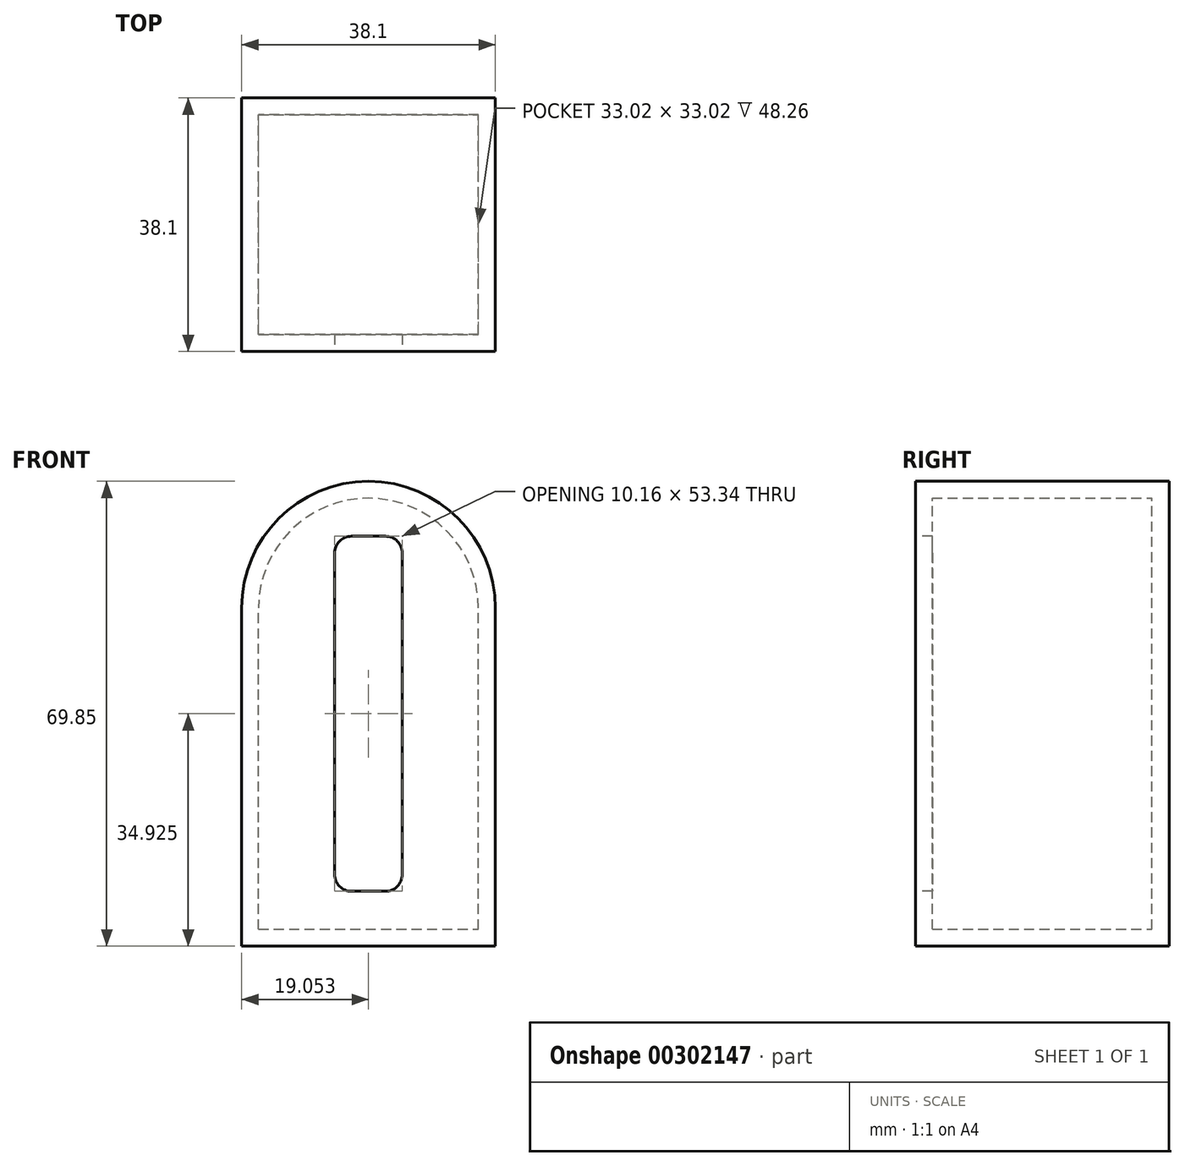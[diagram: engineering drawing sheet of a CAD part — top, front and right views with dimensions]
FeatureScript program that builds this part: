
annotation { "Feature Type Name" : "Feature", "Feature Type Description" : "" }
export const myFeature = defineFeature(function(context is Context, id is Id, definition is map)
    precondition{}
    {
        {
            var Q0;
            Q0=qCreatedBy(makeId("Front.planeOp"),FACE);
            var sketch = newSketch(context, id + "F0", { "sketchPlane" : qUnion([Q0])});
            skLineSegment(sketch, "E0.bottom", {"start": v(-66.24, 0) * mm, "end": v(-28.14, 0) * mm});
            skLineSegment(sketch, "E0.top", {"start": v(-66.24, 50.8) * mm, "end": v(-28.14, 50.8) * mm});
            skLineSegment(sketch, "E0.left", {"start": v(-66.24, 0) * mm, "end": v(-66.24, 50.8) * mm});
            skLineSegment(sketch, "E0.right", {"start": v(-28.14, 0) * mm, "end": v(-28.14, 50.8) * mm});
            skArc(sketch, "E1", {"start": v(-28.14, 50.8) * mm, "mid": v(-47.19, 69.85) * mm, "end": v(-66.24, 50.8) * mm});
            skSolve(sketch);
        }
        {
            var Q0;
            Q0=makeQuery(id+"F0.imprint","IMPRINT",FACE,{"disambiguationData":[TD([[makeQuery(id+"F0.imprint","IMPRINT",EDGE,{"derivedFrom":sQuery(id+"F0.wireOp",EDGE,"E0.bottom")}),1.0]])]});
            var Q1;
            Q1=makeQuery(id+"F0.imprint","IMPRINT",FACE,{"disambiguationData":[TD([[makeQuery(id+"F0.imprint","IMPRINT",EDGE,{"derivedFrom":sQuery(id+"F0.wireOp",EDGE,"E0.top")}),1.0]])]});
            extrude(context, id + "F1", {"entities" : qUnion([Q0, Q1]), "depth" : 38.1 * mm});
        }
        {
            var Q0;
            Q0=makeQuery(id+"F1.opExtrude","CAP_FACE",FACE,{"disambiguationData":[OSD([sQuery(id+"F0.wireOp",EDGE,"E0.bottom"),sQuery(id+"F0.wireOp",EDGE,"E0.left"),sQuery(id+"F0.wireOp",EDGE,"E0.right"),sQuery(id+"F0.wireOp",EDGE,"E1")])],"isStart":false});
            var Q1;
            Q1=makeQuery(id+"F1.opExtrude","SWEPT_BODY",BODY,{"disambiguationData":[OSD([sQuery(id+"F0.wireOp",EDGE,"E0.bottom"),sQuery(id+"F0.wireOp",EDGE,"E0.left"),sQuery(id+"F0.wireOp",EDGE,"E0.right"),sQuery(id+"F0.wireOp",EDGE,"E1")])]});
            shell(context, id + "F2", {"isHollow" : true, "entities" : qUnion([Q0]), "parts" : qUnion([Q1]), "thickness" : 2.54 * mm});
        }
        {
            var Q0;
            Q0=makeQuery(id+"F1.opExtrude","CAP_FACE",FACE,{"disambiguationData":[OSD([sQuery(id+"F0.wireOp",EDGE,"E0.bottom"),sQuery(id+"F0.wireOp",EDGE,"E0.left"),sQuery(id+"F0.wireOp",EDGE,"E0.right"),sQuery(id+"F0.wireOp",EDGE,"E1")])],"isStart":false});
            var sketch = newSketch(context, id + "F3", { "sketchPlane" : qUnion([Q0])});
            skLineSegment(sketch, "E2", {"start": v(-66.24, 0) * mm, "end": v(-28.14, 0) * mm, "construction": true});
            skLineSegment(sketch, "E3", {"start": v(-47.19, 69.85) * mm, "end": v(-47.19, 0) * mm, "construction": true});
            skLineSegment(sketch, "E4.bottom", {"start": v(-44.65, 61.6) * mm, "end": v(-49.73, 61.6) * mm});
            skLineSegment(sketch, "E4.top", {"start": v(-44.65, 8.25) * mm, "end": v(-49.73, 8.25) * mm});
            skLineSegment(sketch, "E4.left", {"start": v(-42.1, 59.06) * mm, "end": v(-42.1, 10.8) * mm});
            skLineSegment(sketch, "E4.right", {"start": v(-52.27, 59.06) * mm, "end": v(-52.27, 10.8) * mm});
            skPoint(sketch, "E4.middle", {"position": v(-47.19, 34.92) * mm});
            skPoint(sketch, "E5.visualSharp", {"position": v(-42.1, 61.6) * mm});
            skArc(sketch, "E5.filletArc", {"start": v(-42.1, 59.06) * mm, "mid": v(-42.85, 60.85) * mm, "end": v(-44.65, 61.6) * mm});
            skPoint(sketch, "E6.visualSharp", {"position": v(-52.27, 61.6) * mm});
            skArc(sketch, "E6.filletArc", {"start": v(-49.73, 61.6) * mm, "mid": v(-51.52, 60.85) * mm, "end": v(-52.27, 59.06) * mm});
            skPoint(sketch, "E7.visualSharp", {"position": v(-42.1, 8.25) * mm});
            skArc(sketch, "E7.filletArc", {"start": v(-44.65, 8.25) * mm, "mid": v(-42.85, 9) * mm, "end": v(-42.1, 10.8) * mm});
            skPoint(sketch, "E8.visualSharp", {"position": v(-52.27, 8.25) * mm});
            skArc(sketch, "E8.filletArc", {"start": v(-52.27, 10.8) * mm, "mid": v(-51.52, 9) * mm, "end": v(-49.73, 8.25) * mm});
            skSolve(sketch);
        }
        {
            var Q0;
            Q0 = qSketchRegion(id + "F3", true);
            extrude(context, id + "F4", {"entities" : qUnion([Q0]), "operationType" : NewBodyOperationType.REMOVE, "oppositeDirection" : true, "depth" : 25.4 * mm});
        }
    });
